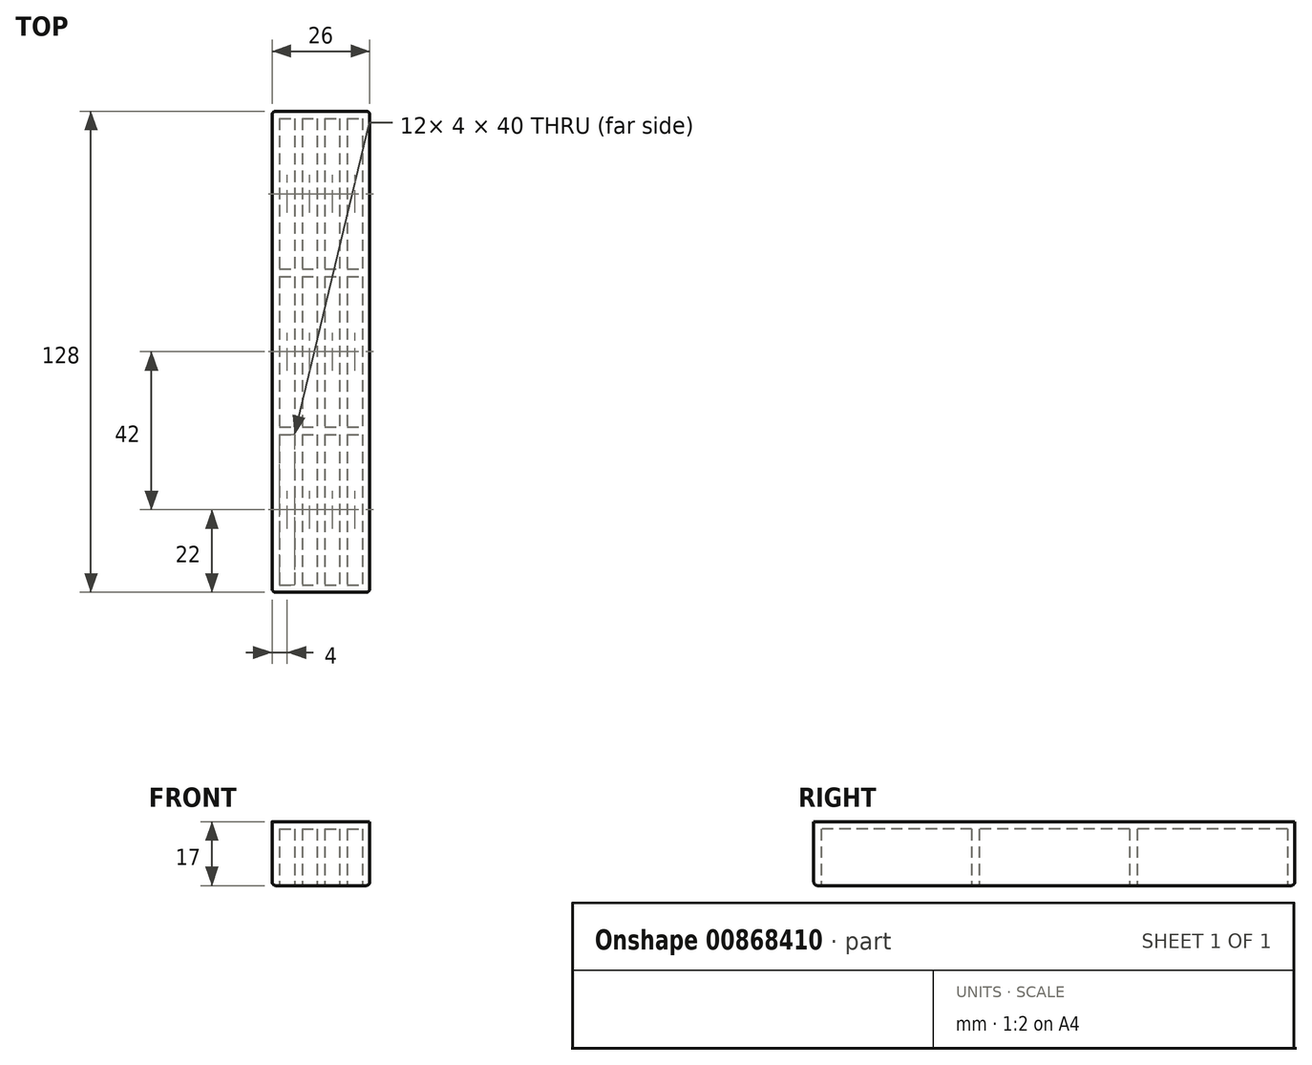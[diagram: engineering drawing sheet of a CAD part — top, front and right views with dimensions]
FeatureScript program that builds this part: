
annotation { "Feature Type Name" : "Feature", "Feature Type Description" : "" }
export const myFeature = defineFeature(function(context is Context, id is Id, definition is map)
    precondition{}
    {
        {
            var Q0;
            Q0=qCreatedBy(makeId("Top.planeOp"),FACE);
            var sketch = newSketch(context, id + "F0", { "sketchPlane" : qUnion([Q0])});
            skLineSegment(sketch, "E0.bottom", {"start": v(-26, 64) * mm, "end": v(0, 64) * mm});
            skLineSegment(sketch, "E0.top", {"start": v(-26, -64) * mm, "end": v(0, -64) * mm});
            skLineSegment(sketch, "E0.left", {"start": v(-26, 64) * mm, "end": v(-26, -64) * mm});
            skLineSegment(sketch, "E0.right", {"start": v(0, 64) * mm, "end": v(0, -64) * mm});
            skSolve(sketch);
        }
        {
            var Q0;
            Q0=makeQuery(id+"F0.imprint","IMPRINT",FACE,{"disambiguationData":[TD([[makeQuery(id+"F0.imprint","IMPRINT",EDGE,{"derivedFrom":sQuery(id+"F0.wireOp",EDGE,"E0.bottom")}),-1.0]])]});
            extrude(context, id + "F1", {"entities" : qUnion([Q0]), "depth" : 17 * mm, "offsetDistance" : 25 * mm});
        }
        {
            var Q0;
            Q0=qCreatedBy(makeId("Top.planeOp"),FACE);
            var sketch = newSketch(context, id + "F2", { "sketchPlane" : qUnion([Q0])});
            skLineSegment(sketch, "E1.bottom", {"start": v(-12, 62) * mm, "end": v(-8, 62) * mm});
            skLineSegment(sketch, "E1.top", {"start": v(-12, 22) * mm, "end": v(-8, 22) * mm});
            skLineSegment(sketch, "E1.left", {"start": v(-12, 62) * mm, "end": v(-12, 22) * mm});
            skLineSegment(sketch, "E1.right", {"start": v(-8, 62) * mm, "end": v(-8, 22) * mm});
            skLineSegment(sketch, "E2.bottom", {"start": v(-6, 62) * mm, "end": v(-2, 62) * mm});
            skLineSegment(sketch, "E2.top", {"start": v(-6, 22) * mm, "end": v(-2, 22) * mm});
            skLineSegment(sketch, "E2.left", {"start": v(-6, 62) * mm, "end": v(-6, 22) * mm});
            skLineSegment(sketch, "E2.right", {"start": v(-2, 62) * mm, "end": v(-2, 22) * mm});
            skLineSegment(sketch, "E3.bottom", {"start": v(-18, 20) * mm, "end": v(-14, 20) * mm});
            skLineSegment(sketch, "E3.top", {"start": v(-18, -20) * mm, "end": v(-14, -20) * mm});
            skLineSegment(sketch, "E3.left", {"start": v(-18, 20) * mm, "end": v(-18, -20) * mm});
            skLineSegment(sketch, "E3.right", {"start": v(-14, 20) * mm, "end": v(-14, -20) * mm});
            skLineSegment(sketch, "E4.bottom", {"start": v(-12, 20) * mm, "end": v(-8, 20) * mm});
            skLineSegment(sketch, "E4.top", {"start": v(-12, -20) * mm, "end": v(-8, -20) * mm});
            skLineSegment(sketch, "E4.left", {"start": v(-12, 20) * mm, "end": v(-12, -20) * mm});
            skLineSegment(sketch, "E4.right", {"start": v(-8, 20) * mm, "end": v(-8, -20) * mm});
            skLineSegment(sketch, "E5.bottom", {"start": v(-6, 20) * mm, "end": v(-2, 20) * mm});
            skLineSegment(sketch, "E5.top", {"start": v(-6, -20) * mm, "end": v(-2, -20) * mm});
            skLineSegment(sketch, "E5.left", {"start": v(-6, 20) * mm, "end": v(-6, -20) * mm});
            skLineSegment(sketch, "E5.right", {"start": v(-2, 20) * mm, "end": v(-2, -20) * mm});
            skLineSegment(sketch, "E6.bottom", {"start": v(-18, -22) * mm, "end": v(-14, -22) * mm});
            skLineSegment(sketch, "E6.top", {"start": v(-18, -62) * mm, "end": v(-14, -62) * mm});
            skLineSegment(sketch, "E6.left", {"start": v(-18, -22) * mm, "end": v(-18, -62) * mm});
            skLineSegment(sketch, "E6.right", {"start": v(-14, -22) * mm, "end": v(-14, -62) * mm});
            skLineSegment(sketch, "E7.bottom", {"start": v(-12, -22) * mm, "end": v(-8, -22) * mm});
            skLineSegment(sketch, "E7.top", {"start": v(-12, -62) * mm, "end": v(-8, -62) * mm});
            skLineSegment(sketch, "E7.left", {"start": v(-12, -22) * mm, "end": v(-12, -62) * mm});
            skLineSegment(sketch, "E7.right", {"start": v(-8, -22) * mm, "end": v(-8, -62) * mm});
            skLineSegment(sketch, "E8.bottom", {"start": v(-6, -22) * mm, "end": v(-2, -22) * mm});
            skLineSegment(sketch, "E8.top", {"start": v(-6, -62) * mm, "end": v(-2, -62) * mm});
            skLineSegment(sketch, "E8.left", {"start": v(-6, -22) * mm, "end": v(-6, -62) * mm});
            skLineSegment(sketch, "E8.right", {"start": v(-2, -22) * mm, "end": v(-2, -62) * mm});
            skLineSegment(sketch, "E9.bottom", {"start": v(-18, 62) * mm, "end": v(-14, 62) * mm});
            skLineSegment(sketch, "E9.top", {"start": v(-18, 22) * mm, "end": v(-14, 22) * mm});
            skLineSegment(sketch, "E9.left", {"start": v(-18, 62) * mm, "end": v(-18, 22) * mm});
            skLineSegment(sketch, "E9.right", {"start": v(-14, 62) * mm, "end": v(-14, 22) * mm});
            skLineSegment(sketch, "E10.bottom", {"start": v(-24, 62) * mm, "end": v(-20, 62) * mm});
            skLineSegment(sketch, "E10.top", {"start": v(-24, 22) * mm, "end": v(-20, 22) * mm});
            skLineSegment(sketch, "E10.left", {"start": v(-24, 62) * mm, "end": v(-24, 22) * mm});
            skLineSegment(sketch, "E10.right", {"start": v(-20, 62) * mm, "end": v(-20, 22) * mm});
            skLineSegment(sketch, "E11.bottom", {"start": v(-24, 20) * mm, "end": v(-20, 20) * mm});
            skLineSegment(sketch, "E11.top", {"start": v(-24, -20) * mm, "end": v(-20, -20) * mm});
            skLineSegment(sketch, "E11.left", {"start": v(-24, 20) * mm, "end": v(-24, -20) * mm});
            skLineSegment(sketch, "E11.right", {"start": v(-20, 20) * mm, "end": v(-20, -20) * mm});
            skLineSegment(sketch, "E12.bottom", {"start": v(-24, -22) * mm, "end": v(-20, -22) * mm});
            skLineSegment(sketch, "E12.top", {"start": v(-24, -62) * mm, "end": v(-20, -62) * mm});
            skLineSegment(sketch, "E12.left", {"start": v(-24, -22) * mm, "end": v(-24, -62) * mm});
            skLineSegment(sketch, "E12.right", {"start": v(-20, -22) * mm, "end": v(-20, -62) * mm});
            skSolve(sketch);
        }
        {
            var Q0;
            Q0 = qSketchRegion(id + "F2", true);
            extrude(context, id + "F3", {"entities" : qUnion([Q0]), "operationType" : NewBodyOperationType.REMOVE, "oppositeDirection" : true, "depth" : -15 * mm, "offsetDistance" : 25 * mm});
        }
        {
            var Q0;
            Q0=makeQuery(id+"F1.opExtrude","CAP_EDGE",EDGE,{"disambiguationData":[OSD([sQuery(id+"F0.wireOp",EDGE,"E0.left")])],"isStart":true});
            var Q1;
            Q1=makeQuery(id+"F1.opExtrude","CAP_EDGE",EDGE,{"disambiguationData":[OSD([sQuery(id+"F0.wireOp",EDGE,"E0.top")])],"isStart":true});
            var Q2;
            Q2=makeQuery(id+"F1.opExtrude","CAP_EDGE",EDGE,{"disambiguationData":[OSD([sQuery(id+"F0.wireOp",EDGE,"E0.right")])],"isStart":true});
            var Q3;
            Q3=makeQuery(id+"F1.opExtrude","CAP_EDGE",EDGE,{"disambiguationData":[OSD([sQuery(id+"F0.wireOp",EDGE,"E0.bottom")])],"isStart":true});
            var Q4;
            Q4=makeQuery(id+"F1.opExtrude","SWEPT_EDGE",EDGE,{"disambiguationData":[OSD([sQuery(id+"F0.wireOp",EDGE,"E0.bottom"),sQuery(id+"F0.wireOp",EDGE,"E0.left")])]});
            var Q5;
            Q5=makeQuery(id+"F1.opExtrude","SWEPT_EDGE",EDGE,{"disambiguationData":[OSD([sQuery(id+"F0.wireOp",EDGE,"E0.bottom"),sQuery(id+"F0.wireOp",EDGE,"E0.right")])]});
            var Q6;
            Q6=makeQuery(id+"F1.opExtrude","SWEPT_EDGE",EDGE,{"disambiguationData":[OSD([sQuery(id+"F0.wireOp",EDGE,"E0.top"),sQuery(id+"F0.wireOp",EDGE,"E0.left")])]});
            var Q7;
            Q7=makeQuery(id+"F1.opExtrude","SWEPT_EDGE",EDGE,{"disambiguationData":[OSD([sQuery(id+"F0.wireOp",EDGE,"E0.top"),sQuery(id+"F0.wireOp",EDGE,"E0.right")])]});
            fillet(context, id + "F4", {"entities" : qUnion([Q0, Q1, Q2, Q3, Q4, Q5, Q6, Q7]), "radius" : 1 * mm, "tangentPropagation" : true, "allowEdgeOverflow" : false});
        }
    });
